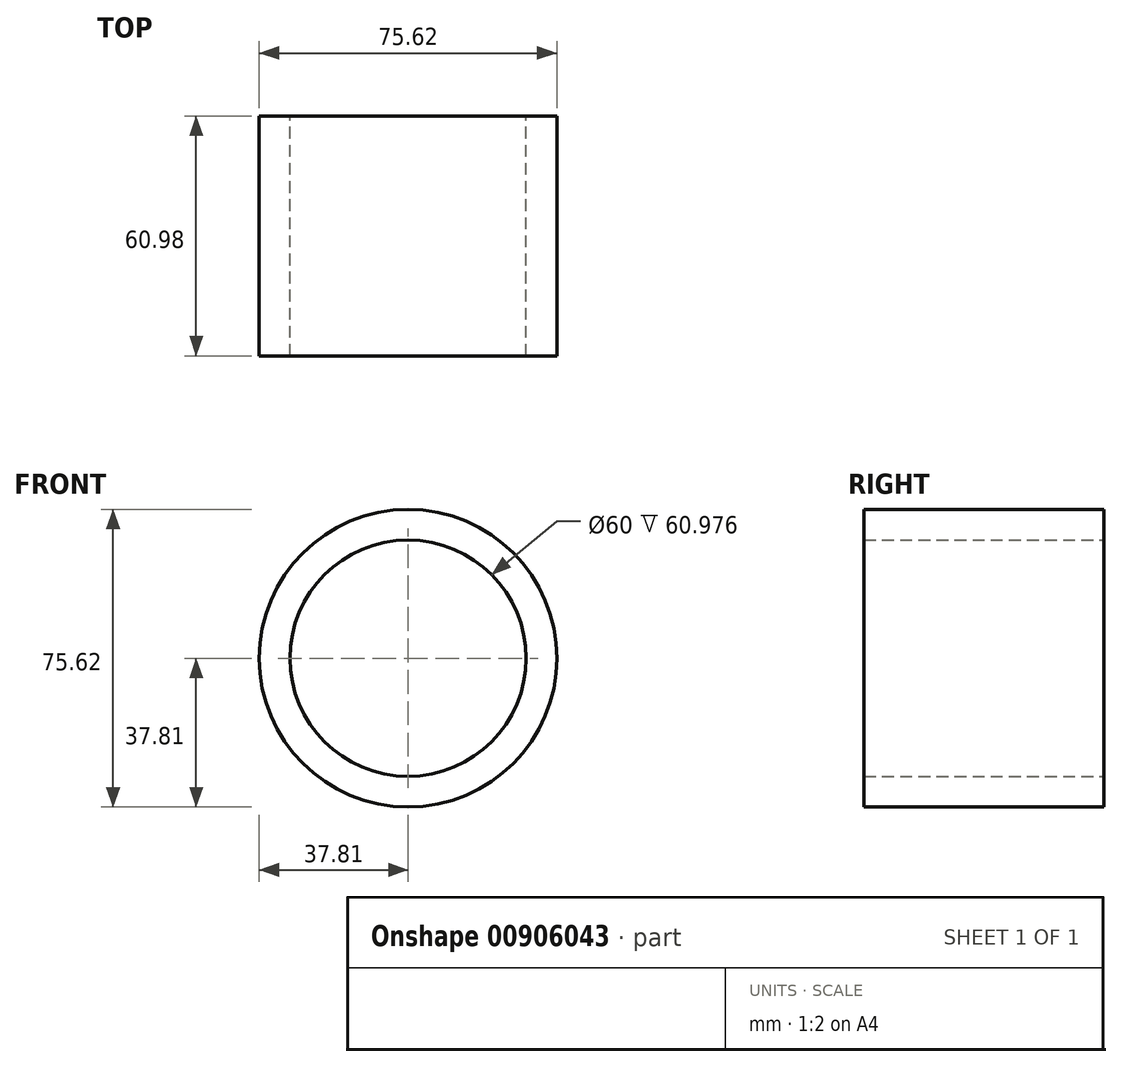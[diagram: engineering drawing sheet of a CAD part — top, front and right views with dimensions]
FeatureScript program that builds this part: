
annotation { "Feature Type Name" : "Feature", "Feature Type Description" : "" }
export const myFeature = defineFeature(function(context is Context, id is Id, definition is map)
    precondition{}
    {
        {
            var Q0;
            Q0=qCreatedBy(makeId("Front.planeOp"),FACE);
            var sketch = newSketch(context, id + "F0", { "sketchPlane" : qUnion([Q0])});
            skCircle(sketch, "E0", {"center": v(0, 0) * mm, "radius": 30 * mm});
            skCircle(sketch, "E1", {"center": v(0, 0) * mm, "radius": 37.81 * mm});
            skSolve(sketch);
        }
        {
            var Q0;
            Q0 = qSketchRegion(id + "F0", true);
            extrude(context, id + "F1", {"entities" : qUnion([Q0]), "depth" : 60.98 * mm, "offsetDistance" : 25 * mm});
        }
    });
